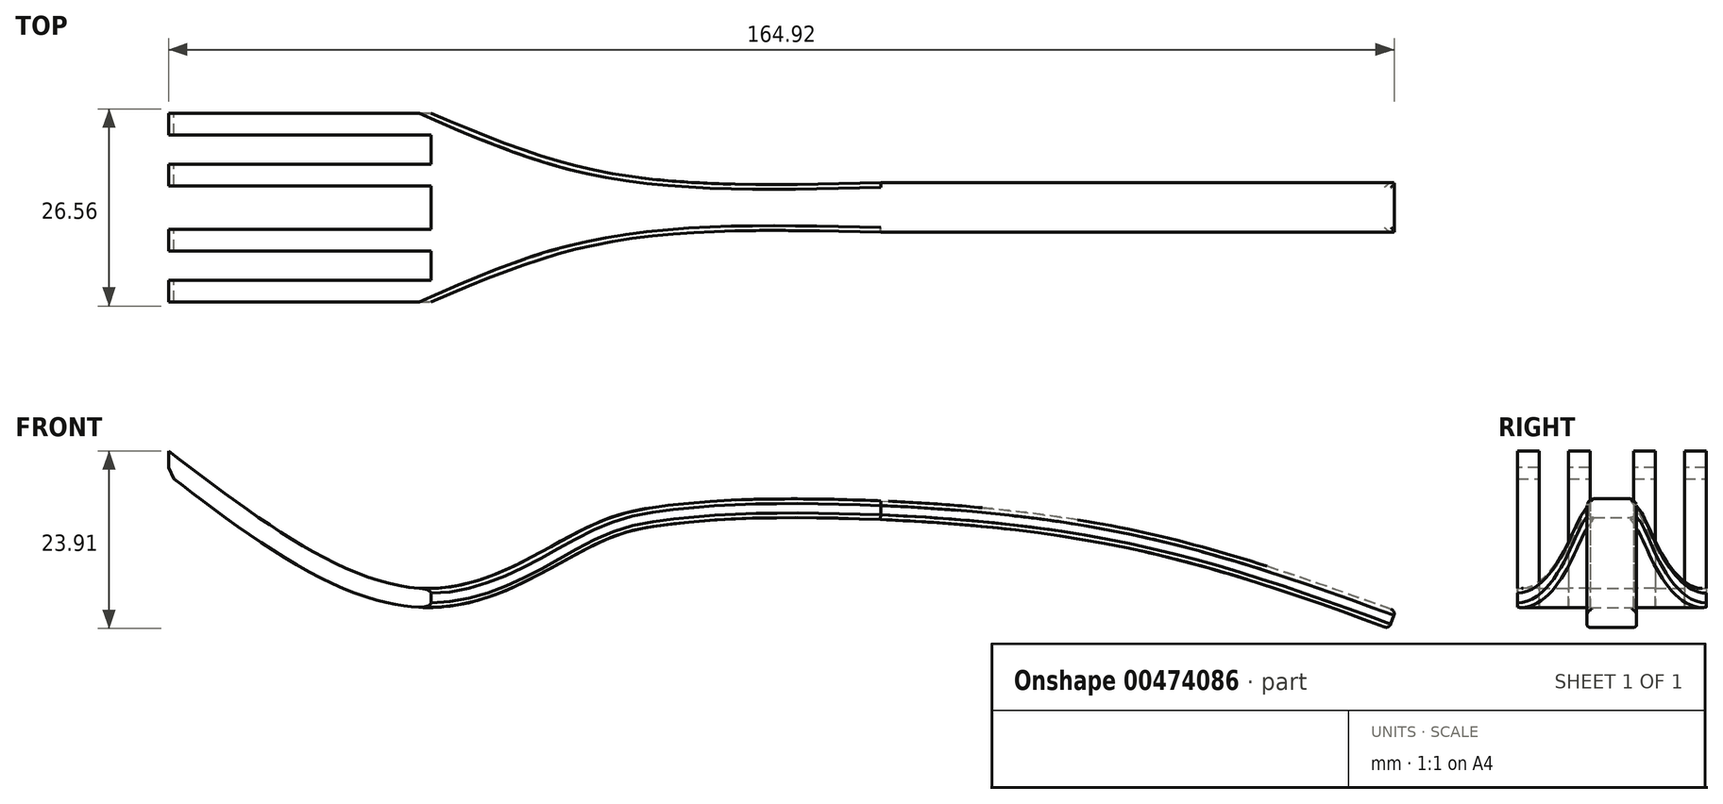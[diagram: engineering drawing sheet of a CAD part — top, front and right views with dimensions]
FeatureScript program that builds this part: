
annotation { "Feature Type Name" : "Feature", "Feature Type Description" : "" }
export const myFeature = defineFeature(function(context is Context, id is Id, definition is map)
    precondition{}
    {
        {
            var Q0;
            Q0=qCreatedBy(makeId("Front.planeOp"),FACE);
            var sketch = newSketch(context, id + "F0", { "sketchPlane" : qUnion([Q0])});
            skFitSpline(sketch, "E0", {"points": [v(0, 0) * mm, v(35.4, -18.5) * mm, v(57.21, -9.86) * mm, v(68.11, -7.23) * mm, v(80.14, -6.48) * mm, v(123.75, -9.49) * mm, v(165.1, -21.52) * mm], "startDerivative": vector(181.56, -138.4) * mm, "endDerivative": vector(185.03, -66.96) * mm});
            skFitSpline(sketch, "E1.0", {"points": [v(-1.54, -2.02) * mm, v(0.35, -3.46) * mm, v(4.15, -6.36) * mm, v(9.86, -10.52) * mm, v(15.56, -14.3) * mm, v(21.25, -17.48) * mm, v(25.99, -19.45) * mm, v(29.79, -20.5) * mm, v(32.17, -20.9) * mm, v(34.08, -21.05) * mm, v(35.5, -21.06) * mm, v(36.92, -20.99) * mm, v(38.77, -20.76) * mm, v(41.02, -20.3) * mm, v(43.6, -19.48) * mm, v(46.06, -18.49) * mm, v(48.41, -17.38) * mm, v(50.65, -16.22) * mm, v(52.78, -15.05) * mm, v(54.79, -13.94) * mm, v(56.35, -13.1) * mm, v(57.53, -12.51) * mm, v(58.37, -12.12) * mm, v(59.19, -11.77) * mm, v(60.24, -11.37) * mm, v(61.52, -10.95) * mm, v(62.98, -10.56) * mm, v(64.41, -10.27) * mm, v(65.82, -10.05) * mm, v(67, -9.9) * mm, v(67.94, -9.8) * mm, v(68.9, -9.7) * mm, v(70.07, -9.58) * mm, v(71.5, -9.45) * mm, v(72.97, -9.33) * mm, v(74.55, -9.22) * mm, v(76.27, -9.13) * mm, v(78.16, -9.06) * mm, v(80.28, -9.01) * mm, v(82.65, -8.99) * mm, v(85.24, -8.99) * mm, v(88.96, -9.03) * mm, v(94.06, -9.16) * mm, v(100.68, -9.48) * mm, v(107.61, -9.99) * mm, v(114.65, -10.7) * mm, v(120.45, -11.5) * mm, v(124.94, -12.26) * mm, v(129.32, -13.12) * mm, v(134.64, -14.33) * mm, v(140.8, -16) * mm, v(146.8, -17.82) * mm, v(154.62, -20.43) * mm, v(160.38, -22.51) * mm, v(164.24, -23.9) * mm]});
            skLineSegment(sketch, "E2", {"start": v(-1.54, -2.02) * mm, "end": v(0, 0) * mm});
            skLineSegment(sketch, "E3", {"start": v(164.24, -23.9) * mm, "end": v(165.1, -21.52) * mm});
            skSolve(sketch);
        }
        {
            var Q0;
            Q0=makeQuery(id+"F0.imprint","IMPRINT",FACE,{"disambiguationData":[TD([[makeQuery(id+"F0.imprint","IMPRINT",EDGE,{"derivedFrom":sQuery(id+"F0.wireOp",EDGE,"E0")}),-1.0]])]});
            extrude(context, id + "F1", {"entities" : qUnion([Q0]), "endBound" : BoundingType.SYMMETRIC, "depth" : 25.4 * mm});
        }
        {
            var Q0;
            Q0=qCreatedBy(makeId("Top.planeOp"),FACE);
            var sketch = newSketch(context, id + "F2", { "sketchPlane" : qUnion([Q0])});
            skLineSegment(sketch, "E4", {"start": v(0, 0) * mm, "end": v(165.1, 0) * mm, "construction": true});
            skPoint(sketch, "E5.0", {"position": v(0, 12.7) * mm});
            skLineSegment(sketch, "E6", {"start": v(0, 12.7) * mm, "end": v(35.32, 12.7) * mm});
            skLineSegment(sketch, "E7", {"start": v(35.32, 9.78) * mm, "end": v(0, 9.78) * mm});
            skLineSegment(sketch, "E8", {"start": v(0, 5.84) * mm, "end": v(35.32, 5.84) * mm});
            skLineSegment(sketch, "E9", {"start": v(35.32, 2.92) * mm, "end": v(0, 2.92) * mm});
            skLineSegment(sketch, "E10", {"start": v(35.32, 2.92) * mm, "end": v(35.32, 0) * mm});
            skLineSegment(sketch, "E11", {"start": v(0, 9.78) * mm, "end": v(0, 12.7) * mm});
            skLineSegment(sketch, "E12", {"start": v(35.32, 5.84) * mm, "end": v(35.32, 9.78) * mm});
            skPoint(sketch, "E13.2.internal.snap0", {"position": v(82.55, 0) * mm});
            skFitSpline(sketch, "E14", {"points": [v(35.32, 12.7) * mm, v(59.45, 4.62) * mm, v(95.83, 3.35) * mm], "startDerivative": vector(49.85, -21.24) * mm, "endDerivative": vector(70.55, 1.85) * mm});
            skLineSegment(sketch, "E15.0", {"start": v(165.1, -12.7) * mm, "end": v(165.1, 12.7) * mm});
            skLineSegment(sketch, "E16", {"start": v(95.83, 3.35) * mm, "end": v(165.1, 3.35) * mm});
            skLineSegment(sketch, "E17.MirrorCS", {"start": v(35.32, -2.92) * mm, "end": v(35.32, 0) * mm});
            skLineSegment(sketch, "E18.MirrorCS", {"start": v(35.32, -5.84) * mm, "end": v(35.32, -9.78) * mm});
            skLineSegment(sketch, "E19.MirrorCS", {"start": v(0, -12.7) * mm, "end": v(35.32, -12.7) * mm});
            skLineSegment(sketch, "E20.MirrorCS", {"start": v(165.1, 12.7) * mm, "end": v(165.1, -12.7) * mm});
            skFitSpline(sketch, "E21.MirrorCS", {"points": [v(35.32, -12.7) * mm, v(59.45, -4.62) * mm, v(95.83, -3.35) * mm], "startDerivative": vector(49.85, 21.24) * mm, "endDerivative": vector(70.55, -1.85) * mm});
            skLineSegment(sketch, "E22.MirrorCS", {"start": v(0, -5.84) * mm, "end": v(35.32, -5.84) * mm});
            skLineSegment(sketch, "E23.MirrorCS", {"start": v(35.32, -2.92) * mm, "end": v(0, -2.92) * mm});
            skPoint(sketch, "E24.MirrorP", {"position": v(0, -12.7) * mm});
            skLineSegment(sketch, "E25.MirrorCS", {"start": v(95.83, -3.35) * mm, "end": v(165.1, -3.35) * mm});
            skLineSegment(sketch, "E26.MirrorCS", {"start": v(35.32, -9.78) * mm, "end": v(0, -9.78) * mm});
            skLineSegment(sketch, "E27.bottom", {"start": v(-9.88, -41.9) * mm, "end": v(178.65, -41.9) * mm});
            skLineSegment(sketch, "E27.top", {"start": v(-9.88, 45.74) * mm, "end": v(178.65, 45.74) * mm});
            skLineSegment(sketch, "E27.left", {"start": v(-9.88, -41.9) * mm, "end": v(-9.88, 45.74) * mm});
            skLineSegment(sketch, "E27.right", {"start": v(178.65, -41.9) * mm, "end": v(178.65, 45.74) * mm});
            skPoint(sketch, "E28.MirrorCS.end.orphan", {"position": v(0, 0) * mm});
            skLineSegment(sketch, "E29", {"start": v(0, 2.92) * mm, "end": v(0, 5.84) * mm});
            skLineSegment(sketch, "E30", {"start": v(0, -2.92) * mm, "end": v(0, -5.84) * mm});
            skLineSegment(sketch, "E31", {"start": v(0, -9.78) * mm, "end": v(0, -12.7) * mm});
            skSolve(sketch);
        }
        {
            var Q0;
            Q0=makeQuery(id+"F2.imprint","IMPRINT",FACE,{"disambiguationData":[TD([[makeQuery(id+"F2.imprint","IMPRINT",EDGE,{"derivedFrom":sQuery(id+"F2.wireOp",EDGE,"E6")}),1.0]])]});
            extrude(context, id + "F3", {"entities" : qUnion([Q0]), "operationType" : NewBodyOperationType.REMOVE, "oppositeDirection" : true, "depth" : 25.4 * mm});
        }
        {
            var Q0;
            Q0=makeQuery(id+"F3.boolean.opBoolean","INTERSECT",EDGE,{"derivedFrom":[makeQuery(id+"F1.opExtrude","SWEPT_FACE",FACE,{"disambiguationData":[OSD([sQuery(id+"F0.wireOp",EDGE,"E1.0")])]}),makeQuery(id+"F3.opExtrude","SWEPT_FACE",FACE,{"disambiguationData":[OSD([sQuery(id+"F2.wireOp",EDGE,"E31")])]})]});
            var Q1;
            Q1=makeQuery(id+"F3.boolean.opBoolean","INTERSECT",EDGE,{"derivedFrom":[makeQuery(id+"F1.opExtrude","SWEPT_FACE",FACE,{"disambiguationData":[OSD([sQuery(id+"F0.wireOp",EDGE,"E1.0")])]}),makeQuery(id+"F3.opExtrude","SWEPT_FACE",FACE,{"disambiguationData":[OSD([sQuery(id+"F2.wireOp",EDGE,"E30")])]})]});
            var Q2;
            Q2=makeQuery(id+"F3.boolean.opBoolean","INTERSECT",EDGE,{"derivedFrom":[makeQuery(id+"F1.opExtrude","SWEPT_FACE",FACE,{"disambiguationData":[OSD([sQuery(id+"F0.wireOp",EDGE,"E1.0")])]}),makeQuery(id+"F3.opExtrude","SWEPT_FACE",FACE,{"disambiguationData":[OSD([sQuery(id+"F2.wireOp",EDGE,"E29")])]})]});
            var Q3;
            Q3=makeQuery(id+"F3.boolean.opBoolean","INTERSECT",EDGE,{"derivedFrom":[makeQuery(id+"F1.opExtrude","SWEPT_FACE",FACE,{"disambiguationData":[OSD([sQuery(id+"F0.wireOp",EDGE,"E1.0")])]}),makeQuery(id+"F3.opExtrude","SWEPT_FACE",FACE,{"disambiguationData":[OSD([sQuery(id+"F2.wireOp",EDGE,"E11")])]})]});
            chamfer(context, id + "F4", {"entities" : qUnion([Q0, Q1, Q2, Q3]), "width" : 1.9 * mm, "tangentPropagation" : true});
        }
        {
            var Q0;
            Q0=makeQuery(id+"F3.boolean.opBoolean","INTERSECT",EDGE,{"derivedFrom":[makeQuery(id+"F1.opExtrude","SWEPT_FACE",FACE,{"disambiguationData":[OSD([sQuery(id+"F0.wireOp",EDGE,"E1.0")])]}),makeQuery(id+"F3.opExtrude","SWEPT_FACE",FACE,{"disambiguationData":[OSD([sQuery(id+"F2.wireOp",EDGE,"E21.MirrorCS")])]})]});
            var Q1;
            Q1=makeQuery(id+"F3.boolean.opBoolean","INTERSECT",EDGE,{"derivedFrom":[makeQuery(id+"F1.opExtrude","SWEPT_FACE",FACE,{"disambiguationData":[OSD([sQuery(id+"F0.wireOp",EDGE,"E1.0")])]}),makeQuery(id+"F3.opExtrude","SWEPT_FACE",FACE,{"disambiguationData":[OSD([sQuery(id+"F2.wireOp",EDGE,"E25.MirrorCS")])]})]});
            var Q2;
            Q2=makeQuery(id+"F3.boolean.opBoolean","INTERSECT",EDGE,{"derivedFrom":[makeQuery(id+"F1.opExtrude","SWEPT_FACE",FACE,{"disambiguationData":[OSD([sQuery(id+"F0.wireOp",EDGE,"E1.0")])]}),makeQuery(id+"F3.opExtrude","SWEPT_FACE",FACE,{"disambiguationData":[OSD([sQuery(id+"F2.wireOp",EDGE,"E14")])]})]});
            var Q3;
            Q3=makeQuery(id+"F3.boolean.opBoolean","INTERSECT",EDGE,{"derivedFrom":[makeQuery(id+"F1.opExtrude","SWEPT_FACE",FACE,{"disambiguationData":[OSD([sQuery(id+"F0.wireOp",EDGE,"E0")])]}),makeQuery(id+"F3.opExtrude","SWEPT_FACE",FACE,{"disambiguationData":[OSD([sQuery(id+"F2.wireOp",EDGE,"E21.MirrorCS")])]})]});
            var Q4;
            Q4=makeQuery(id+"F3.boolean.opBoolean","INTERSECT",EDGE,{"derivedFrom":[makeQuery(id+"F1.opExtrude","SWEPT_FACE",FACE,{"disambiguationData":[OSD([sQuery(id+"F0.wireOp",EDGE,"E0")])]}),makeQuery(id+"F3.opExtrude","SWEPT_FACE",FACE,{"disambiguationData":[OSD([sQuery(id+"F2.wireOp",EDGE,"E25.MirrorCS")])]})]});
            var Q5;
            Q5=makeQuery(id+"F3.boolean.opBoolean","INTERSECT",EDGE,{"derivedFrom":[makeQuery(id+"F1.opExtrude","SWEPT_FACE",FACE,{"disambiguationData":[OSD([sQuery(id+"F0.wireOp",EDGE,"E0")])]}),makeQuery(id+"F3.opExtrude","SWEPT_FACE",FACE,{"disambiguationData":[OSD([sQuery(id+"F2.wireOp",EDGE,"E16")])]})]});
            var Q6;
            Q6=makeQuery(id+"F3.boolean.opBoolean","INTERSECT",EDGE,{"derivedFrom":[makeQuery(id+"F1.opExtrude","SWEPT_FACE",FACE,{"disambiguationData":[OSD([sQuery(id+"F0.wireOp",EDGE,"E0")])]}),makeQuery(id+"F3.opExtrude","SWEPT_FACE",FACE,{"disambiguationData":[OSD([sQuery(id+"F2.wireOp",EDGE,"E14")])]})]});
            var Q7;
            Q7=makeQuery(id+"F1.opExtrude","SWEPT_EDGE",EDGE,{"disambiguationData":[OSD([sQuery(id+"F0.wireOp",EDGE,"E0"),sQuery(id+"F0.wireOp",EDGE,"E3")])]});
            var Q8;
            Q8=makeQuery(id+"F1.opExtrude","SWEPT_EDGE",EDGE,{"disambiguationData":[OSD([sQuery(id+"F0.wireOp",EDGE,"E1.0"),sQuery(id+"F0.wireOp",EDGE,"E3")])]});
            var Q9;
            Q9=makeQuery(id+"F3.boolean.opBoolean","INTERSECT",EDGE,{"derivedFrom":[makeQuery(id+"F1.opExtrude","SWEPT_FACE",FACE,{"disambiguationData":[OSD([sQuery(id+"F0.wireOp",EDGE,"E1.0")])]}),makeQuery(id+"F3.opExtrude","SWEPT_FACE",FACE,{"disambiguationData":[OSD([sQuery(id+"F2.wireOp",EDGE,"E16")])]})]});
            fillet(context, id + "F5", {"entities" : qUnion([Q0, Q1, Q2, Q3, Q4, Q5, Q6, Q7, Q8, Q9]), "radius" : 0.64 * mm, "tangentPropagation" : true, "allowEdgeOverflow" : false});
        }
    });
